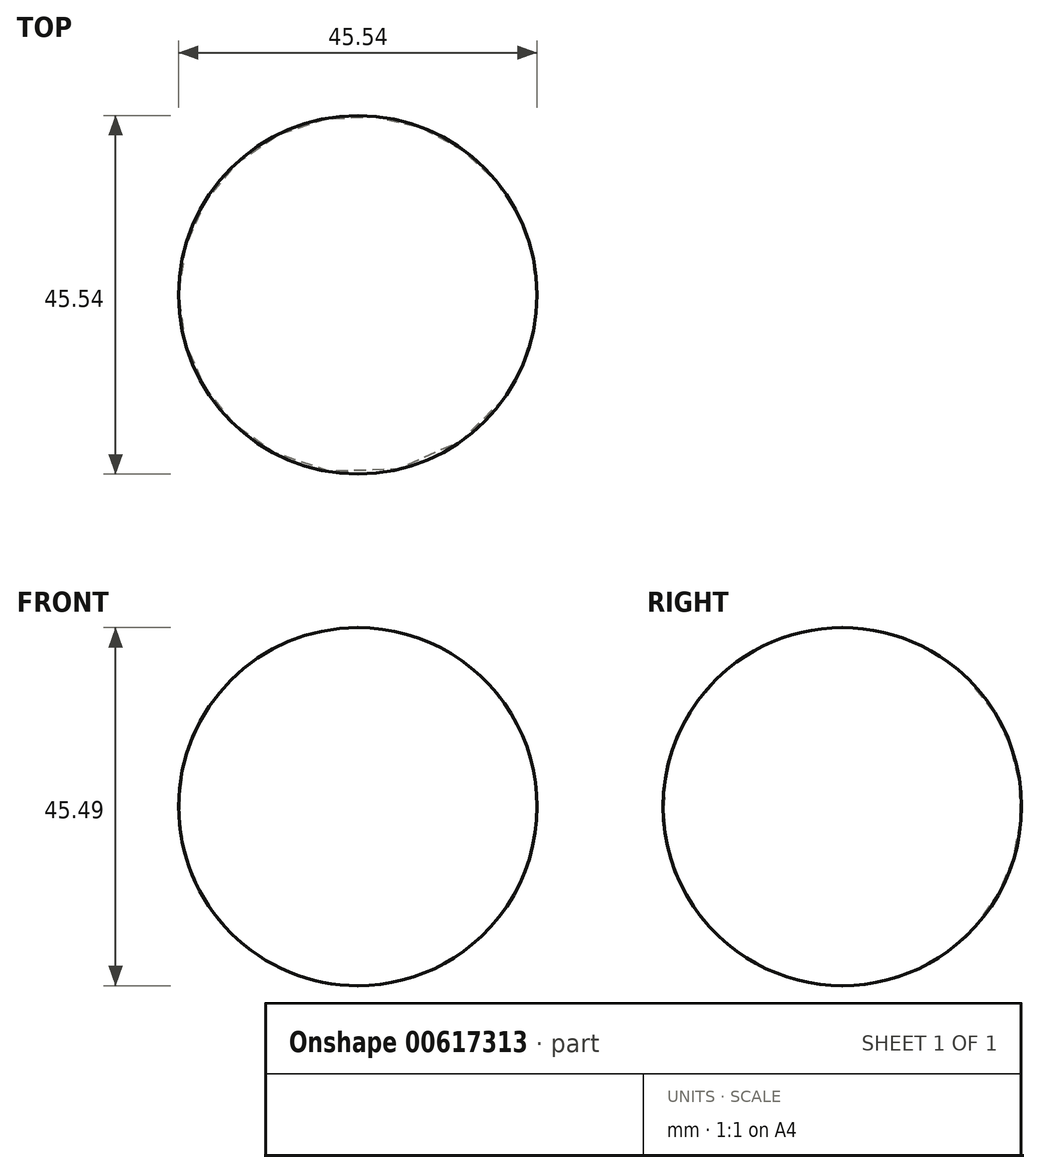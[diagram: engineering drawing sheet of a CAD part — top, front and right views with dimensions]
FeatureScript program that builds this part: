
annotation { "Feature Type Name" : "Feature", "Feature Type Description" : "" }
export const myFeature = defineFeature(function(context is Context, id is Id, definition is map)
    precondition{}
    {
        {
            var Q0;
            Q0=qCreatedBy(makeId("Front.planeOp"),FACE);
            var sketch = newSketch(context, id + "F0", { "sketchPlane" : qUnion([Q0])});
            skLineSegment(sketch, "E0", {"start": v(0, 0) * mm, "end": v(0, 45.49) * mm});
            skArc(sketch, "E1", {"start": v(0, 45.49) * mm, "mid": v(-22.72, 22.74) * mm, "end": v(0, 0) * mm});
            skSolve(sketch);
        }
        {
            var Q0;
            Q0=makeQuery(id+"F0.imprint","IMPRINT",FACE,{"disambiguationData":[TD([[makeQuery(id+"F0.imprint","IMPRINT",EDGE,{"derivedFrom":sQuery(id+"F0.wireOp",EDGE,"E0")}),1.0]])]});
            var Q1;
            Q1=sQuery(id+"F0.wireOp",EDGE,"E0");
            revolve(context, id + "F1", {"entities" : qUnion([Q0]), "axis" : qUnion([Q1]), "revolveType" : RevolveType.FULL});
        }
    });
